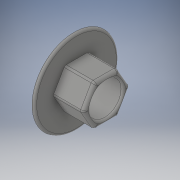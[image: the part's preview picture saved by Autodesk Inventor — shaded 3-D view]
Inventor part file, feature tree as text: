
AUTODESK INVENTOR PART (.ipt)
format: ipt  version: 2017 (Build 210142000, 142)  size: 237,056 bytes
history: native  units: in
note: dims shown in document units (in); Inventor stores cm internally (conversion verified against a paired STEP export)
features: sketch x3, extrude x2, fillet x2, plane x1, hole x1
ambient origin geometry x8: Origin, YZ Plane, XZ Plane, XY Plane, X Axis, Y Axis, Z Axis, Center Point
bodies: Solid1 (feature_tree)
feature tree (9):
  plane  "Work Plane1"
  extrude  "Screw_head"  Depth=0.5118in TaperAngle=0.0deg
  extrude  "Extrusion7"  Depth=1.4173in
  hole  "Hole2"  [1 undecoded]
  fillet  "Fillet3"  Radius=0.0394in
  fillet  "Fillet4"  Radius=0.5512in
  sketch  "Sketch3"  dims[d0=0.7874in d7=0.5118in d8=0.0in]
  sketch  "Sketch8"  dims[d28=0.7874in d38=1.4173in]
  sketch  "Sketch12"  dims[d39=0.0591in d40=0.0in d61=0.0591in d71=0.0394in d72=0.5512in d73=0.5512in d74=0.2953in d75=0.1476in d76=0.0984in d77=90.0deg d78=0.3937in d79=0.8108in]
note: 1 required parameter value undecoded (feature->parameter linkage not recoverable at this tier; creation-order binding heuristic only, values carry confidence <= 0.55)
